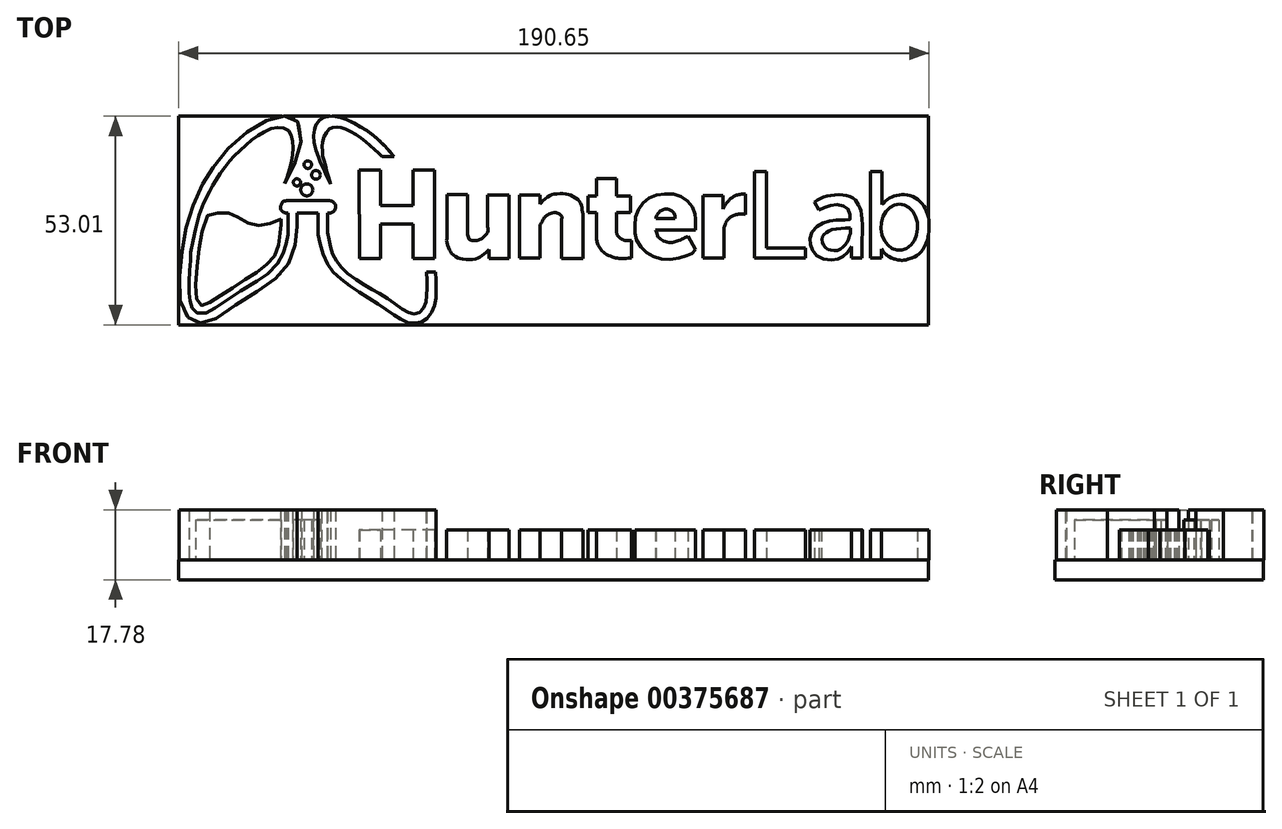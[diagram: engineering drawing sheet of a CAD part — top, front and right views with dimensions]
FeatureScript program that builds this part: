
annotation { "Feature Type Name" : "Feature", "Feature Type Description" : "" }
export const myFeature = defineFeature(function(context is Context, id is Id, definition is map)
    precondition{}
    {
        {
            var Q0;
            Q0=qCreatedBy(makeId("Top.planeOp"),FACE);
            var sketch = newSketch(context, id + "F0", { "sketchPlane" : qUnion([Q0])});
            skLineSegment(sketch, "E0.bottom", {"start": v(-95.8, -13.92) * mm, "end": v(94.76, -13.92) * mm});
            skLineSegment(sketch, "E0.top", {"start": v(-95.8, 39.08) * mm, "end": v(94.76, 39.08) * mm});
            skLineSegment(sketch, "E0.left", {"start": v(-95.8, -13.92) * mm, "end": v(-95.8, 39.08) * mm});
            skLineSegment(sketch, "E0.right", {"start": v(94.76, -13.92) * mm, "end": v(94.76, 39.08) * mm});
            skSolve(sketch);
        }
        {
            var Q0;
            Q0 = qSketchRegion(id + "F0", true);
            extrude(context, id + "F1", {"entities" : qUnion([Q0]), "oppositeDirection" : true, "depth" : 5.08 * mm});
        }
        {
            var Q0;
            Q0=qCreatedBy(makeId("Top.planeOp"),FACE);
            var sketch = newSketch(context, id + "F2", { "sketchPlane" : qUnion([Q0])});
            skLineSegment(sketch, "E1", {"start": v(-49.96, 25.38) * mm, "end": v(-44.45, 25.38) * mm});
            skLineSegment(sketch, "E2", {"start": v(-44.45, 25.38) * mm, "end": v(-44.45, 16.38) * mm});
            skLineSegment(sketch, "E3", {"start": v(-44.45, 16.38) * mm, "end": v(-36.19, 16.38) * mm});
            skLineSegment(sketch, "E4", {"start": v(-36.19, 16.38) * mm, "end": v(-36.19, 25.38) * mm});
            skLineSegment(sketch, "E5", {"start": v(-36.19, 25.38) * mm, "end": v(-30.8, 25.38) * mm});
            skLineSegment(sketch, "E6", {"start": v(-30.8, 25.38) * mm, "end": v(-30.8, 2.94) * mm});
            skLineSegment(sketch, "E7", {"start": v(-30.8, 2.94) * mm, "end": v(-36.19, 2.94) * mm});
            skLineSegment(sketch, "E8", {"start": v(-36.19, 2.94) * mm, "end": v(-36.19, 11.68) * mm});
            skLineSegment(sketch, "E9", {"start": v(-36.19, 11.68) * mm, "end": v(-44.45, 11.68) * mm});
            skLineSegment(sketch, "E10", {"start": v(-44.45, 11.68) * mm, "end": v(-44.45, 2.94) * mm});
            skLineSegment(sketch, "E11", {"start": v(-44.45, 2.94) * mm, "end": v(-49.84, 2.94) * mm});
            skLineSegment(sketch, "E12", {"start": v(-49.84, 2.94) * mm, "end": v(-49.96, 25.38) * mm});
            skLineSegment(sketch, "E13", {"start": v(-22.34, 19.15) * mm, "end": v(-27.62, 19.15) * mm});
            skLineSegment(sketch, "E14", {"start": v(-27.62, 19.15) * mm, "end": v(-27.62, 7.97) * mm});
            skLineSegment(sketch, "E15", {"start": v(-22.34, 19.15) * mm, "end": v(-22.34, 9.02) * mm});
            skLineSegment(sketch, "E16", {"start": v(-17.24, 10.98) * mm, "end": v(-17.24, 19.09) * mm});
            skLineSegment(sketch, "E17", {"start": v(-17.24, 19.09) * mm, "end": v(-11.9, 19.09) * mm});
            skLineSegment(sketch, "E18", {"start": v(-11.9, 19.09) * mm, "end": v(-11.9, 2.93) * mm});
            skLineSegment(sketch, "E19", {"start": v(-11.9, 2.93) * mm, "end": v(-16.94, 2.93) * mm});
            skLineSegment(sketch, "E20", {"start": v(-16.94, 2.93) * mm, "end": v(-16.94, 5.2) * mm});
            skLineSegment(sketch, "E21", {"start": v(-3.91, 16.75) * mm, "end": v(-3.91, 19.03) * mm});
            skLineSegment(sketch, "E22", {"start": v(-3.91, 19.03) * mm, "end": v(-9.13, 19.03) * mm});
            skLineSegment(sketch, "E23", {"start": v(-9.13, 19.03) * mm, "end": v(-9.13, 3) * mm});
            skLineSegment(sketch, "E24", {"start": v(-9.13, 3) * mm, "end": v(-3.91, 3) * mm});
            skLineSegment(sketch, "E25", {"start": v(-3.91, 3) * mm, "end": v(-3.91, 11.53) * mm});
            skLineSegment(sketch, "E26", {"start": v(1.55, 12.95) * mm, "end": v(1.55, 2.93) * mm});
            skLineSegment(sketch, "E27", {"start": v(1.55, 2.93) * mm, "end": v(6.9, 2.93) * mm});
            skLineSegment(sketch, "E28", {"start": v(6.9, 2.93) * mm, "end": v(6.9, 14.18) * mm});
            skLineSegment(sketch, "E29", {"start": v(15.5, 9.36) * mm, "end": v(15.5, 14.66) * mm});
            skLineSegment(sketch, "E30", {"start": v(15.5, 14.66) * mm, "end": v(19, 14.66) * mm});
            skLineSegment(sketch, "E31", {"start": v(19, 14.66) * mm, "end": v(19, 18.73) * mm});
            skLineSegment(sketch, "E32", {"start": v(19, 18.73) * mm, "end": v(15.5, 18.73) * mm});
            skLineSegment(sketch, "E33", {"start": v(15.5, 18.73) * mm, "end": v(15.5, 23.29) * mm});
            skLineSegment(sketch, "E34", {"start": v(15.5, 23.29) * mm, "end": v(10.42, 23.29) * mm});
            skLineSegment(sketch, "E35", {"start": v(10.42, 23.29) * mm, "end": v(10.42, 18.73) * mm});
            skLineSegment(sketch, "E36", {"start": v(10.42, 18.73) * mm, "end": v(8.22, 18.73) * mm});
            skLineSegment(sketch, "E37", {"start": v(8.22, 18.73) * mm, "end": v(8.22, 14.66) * mm});
            skLineSegment(sketch, "E38", {"start": v(8.22, 14.66) * mm, "end": v(10.42, 14.66) * mm});
            skLineSegment(sketch, "E39", {"start": v(10.42, 14.66) * mm, "end": v(10.42, 7.8) * mm});
            skLineSegment(sketch, "E40", {"start": v(19.22, 7.53) * mm, "end": v(19.22, 3.01) * mm});
            skLineSegment(sketch, "E41", {"start": v(25.43, 10.11) * mm, "end": v(35.5, 10.11) * mm});
            skLineSegment(sketch, "E42", {"start": v(35.5, 10.11) * mm, "end": v(35.5, 13.01) * mm});
            skLineSegment(sketch, "E43", {"start": v(25.48, 13.06) * mm, "end": v(30.32, 13.06) * mm});
            skLineSegment(sketch, "E44", {"start": v(33.65, 8.61) * mm, "end": v(35.56, 5.18) * mm});
            skLineSegment(sketch, "E45", {"start": v(42.73, 10.52) * mm, "end": v(42.73, 2.99) * mm});
            skLineSegment(sketch, "E46", {"start": v(42.73, 2.99) * mm, "end": v(37.44, 2.99) * mm});
            skLineSegment(sketch, "E47", {"start": v(37.44, 2.99) * mm, "end": v(37.44, 18.97) * mm});
            skLineSegment(sketch, "E48", {"start": v(37.44, 18.97) * mm, "end": v(42.48, 18.97) * mm});
            skLineSegment(sketch, "E49", {"start": v(42.48, 18.97) * mm, "end": v(42.48, 15.46) * mm});
            skLineSegment(sketch, "E50", {"start": v(48.23, 19.32) * mm, "end": v(48.23, 14.13) * mm});
            skLineSegment(sketch, "E51", {"start": v(50.52, 24.97) * mm, "end": v(53.57, 24.97) * mm});
            skLineSegment(sketch, "E52", {"start": v(53.57, 24.97) * mm, "end": v(53.57, 5.64) * mm});
            skLineSegment(sketch, "E53", {"start": v(53.57, 5.64) * mm, "end": v(63.45, 5.64) * mm});
            skLineSegment(sketch, "E54", {"start": v(63.45, 5.64) * mm, "end": v(63.45, 2.99) * mm});
            skLineSegment(sketch, "E55", {"start": v(63.45, 2.99) * mm, "end": v(50.52, 2.99) * mm});
            skLineSegment(sketch, "E56", {"start": v(50.52, 2.99) * mm, "end": v(50.52, 24.97) * mm});
            skLineSegment(sketch, "E57", {"start": v(65.79, 17.29) * mm, "end": v(66.85, 15.2) * mm});
            skLineSegment(sketch, "E58", {"start": v(75.17, 2.99) * mm, "end": v(77.8, 2.99) * mm});
            skLineSegment(sketch, "E59", {"start": v(82.93, 24.97) * mm, "end": v(79.98, 24.97) * mm});
            skLineSegment(sketch, "E60", {"start": v(79.98, 24.97) * mm, "end": v(79.98, 2.99) * mm});
            skLineSegment(sketch, "E61", {"start": v(79.98, 2.99) * mm, "end": v(82.78, 2.99) * mm});
            skLineSegment(sketch, "E62", {"start": v(82.78, 2.99) * mm, "end": v(82.78, 5.28) * mm});
            skLineSegment(sketch, "E63", {"start": v(82.93, 24.97) * mm, "end": v(82.93, 16.58) * mm});
            skFitSpline(sketch, "E64", {"points": [v(82.93, 16.58) * mm, v(84.56, 18.15) * mm, v(86.65, 18.97) * mm, v(89.2, 19.07) * mm, v(91.94, 17.95) * mm, v(93.88, 15.66) * mm, v(94.86, 12.7) * mm, v(94.86, 9.8) * mm, v(94.33, 7.26) * mm, v(92.7, 4.52) * mm, v(91.03, 3.3) * mm, v(88.18, 2.48) * mm, v(85.89, 2.84) * mm, v(84.1, 3.8) * mm, v(82.78, 5.28) * mm], "startDerivative": vector(22.65, 26) * mm, "endDerivative": vector(-19.5, 25.28) * mm});
            skEllipse(sketch, "E65", {"center": v(87.31, 10.88) * mm, "majorRadius": 5.87 * mm, "minorRadius": 4.66 * mm, "majorAxis": v(0, 1)});
            skFitSpline(sketch, "E66", {"points": [v(65.79, 17.29) * mm, v(67.57, 18.3) * mm, v(69.96, 18.97) * mm, v(72.96, 19.07) * mm, v(75.15, 18.46) * mm, v(76.52, 17.29) * mm, v(77.27, 15.83) * mm, v(77.8, 13.58) * mm, v(77.8, 2.99) * mm], "startDerivative": vector(16.24, 10.48) * mm, "endDerivative": vector(-0.09, -55.71) * mm});
            skFitSpline(sketch, "E67", {"points": [v(66.85, 15.2) * mm, v(68.62, 16) * mm, v(70.4, 16.52) * mm, v(72.6, 16.46) * mm, v(74.07, 15.68) * mm, v(74.75, 14.31) * mm, v(74.8, 12.9) * mm, v(74.23, 12.74) * mm, v(71.19, 12.74) * mm, v(68.93, 12.32) * mm, v(66.85, 11.43) * mm, v(65.16, 9.64) * mm, v(64.63, 7.55) * mm, v(64.84, 5.92) * mm, v(65.78, 4.19) * mm, v(68.1, 2.82) * mm, v(70.93, 2.61) * mm, v(72.66, 3.24) * mm, v(73.81, 4.08) * mm, v(75.17, 5.92) * mm], "startDerivative": vector(33.79, 15.82) * mm, "endDerivative": vector(21.23, 32.82) * mm});
            skLineSegment(sketch, "E68", {"start": v(75.17, 5.92) * mm, "end": v(75.17, 2.99) * mm});
            skFitSpline(sketch, "E69", {"points": [v(74.91, 10.64) * mm, v(71.76, 10.48) * mm, v(69.56, 10.01) * mm, v(68.56, 9.33) * mm, v(67.83, 8.54) * mm, v(67.67, 7.34) * mm, v(68.1, 6.29) * mm, v(69.09, 5.34) * mm, v(70.2, 5.03) * mm, v(71.71, 5.03) * mm, v(72.81, 5.66) * mm, v(73.81, 6.65) * mm, v(74.5, 8.02) * mm, v(74.91, 9.33) * mm, v(74.91, 9.28) * mm], "startDerivative": vector(-28.78, -0.8) * mm, "endDerivative": vector(-4.05, -5.26) * mm});
            skLineSegment(sketch, "E70", {"start": v(74.91, 10.64) * mm, "end": v(74.91, 9.33) * mm});
            skFitSpline(sketch, "E71", {"points": [v(42.48, 15.46) * mm, v(43.53, 17.16) * mm, v(44.95, 18.46) * mm, v(46.25, 19.08) * mm, v(48.23, 19.32) * mm], "startDerivative": vector(3.6, 6.76) * mm, "endDerivative": vector(8.08, 0.55) * mm});
            skFitSpline(sketch, "E72", {"points": [v(48.23, 14.13) * mm, v(46.07, 14.13) * mm, v(44.52, 13.5) * mm, v(43.28, 12.14) * mm, v(42.73, 10.52) * mm], "startDerivative": vector(-8.11, 0.9) * mm, "endDerivative": vector(-2.19, -5.73) * mm});
            skFitSpline(sketch, "E73", {"points": [v(35.5, 13.01) * mm, v(35.5, 14) * mm, v(34.49, 16.41) * mm, v(32.63, 18.21) * mm, v(29.9, 19.26) * mm, v(26.62, 19.2) * mm, v(23.71, 18.27) * mm, v(21.73, 16.41) * mm, v(20.3, 13.69) * mm, v(20.12, 10.66) * mm, v(20.37, 8.24) * mm, v(21.8, 5.64) * mm, v(23.96, 3.84) * mm, v(26.87, 2.8) * mm, v(30.28, 2.8) * mm, v(33.62, 3.72) * mm, v(34.61, 4.21) * mm, v(35.56, 5.18) * mm], "startDerivative": vector(2.92, 23.87) * mm, "endDerivative": vector(15.92, 25.8) * mm});
            skFitSpline(sketch, "E74", {"points": [v(33.65, 8.61) * mm, v(32.38, 8) * mm, v(31.02, 7.37) * mm, v(29.84, 7.06) * mm, v(28.3, 7.06) * mm, v(26.93, 7.68) * mm, v(25.94, 8.61) * mm, v(25.43, 10.11) * mm], "startDerivative": vector(-8.12, -5.44) * mm, "endDerivative": vector(-4.59, 9.54) * mm});
            skFitSpline(sketch, "E75", {"points": [v(15.5, 9.36) * mm, v(15.79, 8.67) * mm, v(16.73, 7.86) * mm, v(17.84, 7.5) * mm, v(19.22, 7.53) * mm], "startDerivative": vector(0.88, -3.35) * mm, "endDerivative": vector(5.13, 0.44) * mm});
            skFitSpline(sketch, "E76", {"points": [v(10.42, 7.8) * mm, v(10.62, 6.68) * mm, v(11.4, 5.33) * mm, v(12.66, 4.15) * mm, v(14.64, 3.27) * mm, v(16.09, 2.98) * mm, v(19.22, 3.01) * mm], "startDerivative": vector(0.64, -8.95) * mm, "endDerivative": vector(16.04, 0.67) * mm});
            skFitSpline(sketch, "E77", {"points": [v(-3.91, 16.75) * mm, v(-3.07, 17.74) * mm, v(-1.3, 18.95) * mm, v(0, 19.3) * mm, v(2.44, 19.35) * mm, v(3.95, 18.95) * mm, v(5.72, 17.79) * mm, v(6.42, 16.75) * mm, v(6.73, 15.42) * mm, v(6.9, 14.18) * mm], "startDerivative": vector(7.09, 9.57) * mm, "endDerivative": vector(1.61, -12.4) * mm});
            skFitSpline(sketch, "E78", {"points": [v(1.55, 12.95) * mm, v(1.55, 13.65) * mm, v(1.02, 14.18) * mm, v(0, 14.6) * mm, v(-1.75, 14.18) * mm, v(-2.56, 13.65) * mm, v(-3.12, 12.95) * mm, v(-3.42, 12.24) * mm, v(-3.91, 11.53) * mm], "startDerivative": vector(1.14, 7.02) * mm, "endDerivative": vector(-4.71, -5.81) * mm});
            skFitSpline(sketch, "E79", {"points": [v(-17.24, 10.98) * mm, v(-17.24, 9.86) * mm, v(-18.25, 8.41) * mm, v(-19.13, 7.8) * mm, v(-20.35, 7.46) * mm, v(-21.23, 7.5) * mm, v(-21.92, 7.8) * mm, v(-22.34, 9.02) * mm], "startDerivative": vector(1.28, -7.5) * mm, "endDerivative": vector(-1.92, 8.98) * mm});
            skFitSpline(sketch, "E80", {"points": [v(-27.62, 7.97) * mm, v(-27.62, 6.84) * mm, v(-27, 5.23) * mm, v(-26.42, 4.25) * mm, v(-25.07, 3.2) * mm, v(-23.4, 2.77) * mm, v(-20.58, 2.77) * mm, v(-19.03, 3.4) * mm, v(-17.72, 4.44) * mm, v(-16.94, 5.2) * mm], "startDerivative": vector(-1.32, -11.42) * mm, "endDerivative": vector(7.85, 7.93) * mm});
            skFitSpline(sketch, "E81", {"points": [v(25.48, 13.06) * mm, v(25.72, 13.85) * mm, v(26.5, 14.87) * mm, v(27.26, 15.33) * mm, v(28.05, 15.46) * mm, v(28.92, 15.35) * mm, v(29.6, 14.95) * mm, v(30.16, 14.22) * mm, v(30.32, 13.56) * mm, v(30.32, 13.06) * mm], "startDerivative": vector(1.4, 6.81) * mm, "endDerivative": vector(-0.2, -5.58) * mm});
            skLineSegment(sketch, "E82.bottom", {"start": v(-95.64, 39.01) * mm, "end": v(94.86, 39.01) * mm});
            skLineSegment(sketch, "E82.top", {"start": v(-95.64, -13.6) * mm, "end": v(94.86, -13.6) * mm});
            skLineSegment(sketch, "E82.left", {"start": v(-95.64, 39.01) * mm, "end": v(-95.64, -13.6) * mm});
            skLineSegment(sketch, "E82.right", {"start": v(94.86, 39.01) * mm, "end": v(94.86, -13.6) * mm});
            skSolve(sketch);
        }
        {
            var Q0;
            Q0=makeQuery(id+"F2.imprint","IMPRINT",FACE,{"disambiguationData":[TD([[makeQuery(id+"F2.imprint","IMPRINT",EDGE,{"derivedFrom":sQuery(id+"F2.wireOp",EDGE,"E1")}),-1.0]])]});
            var Q1;
            Q1=makeQuery(id+"F2.imprint","IMPRINT",FACE,{"disambiguationData":[TD([[makeQuery(id+"F2.imprint","IMPRINT",EDGE,{"derivedFrom":sQuery(id+"F2.wireOp",EDGE,"E13")}),1.0]])]});
            var Q2;
            Q2=makeQuery(id+"F2.imprint","IMPRINT",FACE,{"disambiguationData":[TD([[makeQuery(id+"F2.imprint","IMPRINT",EDGE,{"derivedFrom":sQuery(id+"F2.wireOp",EDGE,"E21")}),1.0]])]});
            var Q3;
            Q3=makeQuery(id+"F2.imprint","IMPRINT",FACE,{"disambiguationData":[TD([[makeQuery(id+"F2.imprint","IMPRINT",EDGE,{"derivedFrom":sQuery(id+"F2.wireOp",EDGE,"E29")}),1.0]])]});
            var Q4;
            Q4=makeQuery(id+"F2.imprint","IMPRINT",FACE,{"disambiguationData":[TD([[makeQuery(id+"F2.imprint","IMPRINT",EDGE,{"derivedFrom":sQuery(id+"F2.wireOp",EDGE,"E45")}),-1.0]])]});
            var Q5;
            Q5=makeQuery(id+"F2.imprint","IMPRINT",FACE,{"disambiguationData":[TD([[makeQuery(id+"F2.imprint","IMPRINT",EDGE,{"derivedFrom":sQuery(id+"F2.wireOp",EDGE,"E41")}),1.0]])]});
            extrude(context, id + "F3", {"entities" : qUnion([Q0, Q1, Q2, Q3, Q4, Q5]), "operationType" : NewBodyOperationType.ADD, "depth" : 7.62 * mm});
        }
        {
            var Q0;
            Q0=makeQuery(id+"F2.imprint","IMPRINT",FACE,{"disambiguationData":[TD([[makeQuery(id+"F2.imprint","IMPRINT",EDGE,{"derivedFrom":sQuery(id+"F2.wireOp",EDGE,"E51")}),-1.0]])]});
            var Q1;
            Q1=makeQuery(id+"F2.imprint","IMPRINT",FACE,{"disambiguationData":[TD([[makeQuery(id+"F2.imprint","IMPRINT",EDGE,{"derivedFrom":sQuery(id+"F2.wireOp",EDGE,"E57")}),1.0]])]});
            var Q2;
            Q2=makeQuery(id+"F2.imprint","IMPRINT",FACE,{"disambiguationData":[TD([[makeQuery(id+"F2.imprint","IMPRINT",EDGE,{"derivedFrom":sQuery(id+"F2.wireOp",EDGE,"E59")}),1.0]])]});
            extrude(context, id + "F4", {"entities" : qUnion([Q0, Q1, Q2]), "operationType" : NewBodyOperationType.ADD, "depth" : 7.62 * mm});
        }
        {
            var Q0;
            Q0=makeQuery(id+"F2.imprint","IMPRINT",FACE,{"disambiguationData":[TD([[makeQuery(id+"F2.imprint","IMPRINT",EDGE,{"derivedFrom":sQuery(id+"F2.wireOp",EDGE,"E1")}),1.0]])]});
            var sketch = newSketch(context, id + "F5", { "sketchPlane" : qUnion([Q0])});
            skLineSegment(sketch, "E83", {"start": v(-68.34, 17.61) * mm, "end": v(-58.06, 17.61) * mm});
            skLineSegment(sketch, "E84", {"start": v(-67.95, 14.5) * mm, "end": v(-67.95, 11.06) * mm});
            skLineSegment(sketch, "E85", {"start": v(-57.94, 14.5) * mm, "end": v(-57.94, 11.36) * mm});
            skLineSegment(sketch, "E86", {"start": v(-65.7, 11.06) * mm, "end": v(-65.7, 14.5) * mm});
            skLineSegment(sketch, "E87", {"start": v(-65.7, 14.5) * mm, "end": v(-60.32, 14.5) * mm});
            skLineSegment(sketch, "E88", {"start": v(-60.32, 14.5) * mm, "end": v(-60.32, 11.26) * mm});
            skFitSpline(sketch, "E89", {"points": [v(-68.34, 17.61) * mm, v(-69.09, 17.46) * mm, v(-69.64, 16.83) * mm, v(-69.86, 16.05) * mm, v(-69.83, 15.46) * mm, v(-69.42, 14.87) * mm, v(-68.72, 14.54) * mm, v(-67.95, 14.5) * mm], "startDerivative": vector(-5.2, -2.07) * mm, "endDerivative": vector(5.37, 0.05) * mm});
            skFitSpline(sketch, "E90", {"points": [v(-57.94, 14.5) * mm, v(-57.16, 14.5) * mm, v(-56.52, 14.8) * mm, v(-56.05, 15.33) * mm, v(-55.97, 16.62) * mm, v(-56.3, 17.09) * mm, v(-56.85, 17.45) * mm, v(-57.46, 17.61) * mm, v(-58.06, 17.61) * mm], "startDerivative": vector(6.89, -0.67) * mm, "endDerivative": vector(-5.35, -0.27) * mm});
            skFitSpline(sketch, "E91", {"points": [v(-67.95, 11.06) * mm, v(-67.95, 9.88) * mm, v(-68.13, 8.36) * mm, v(-68.56, 6.34) * mm, v(-69.12, 4.33) * mm, v(-70.12, 2.36) * mm, v(-73.05, -0.87) * mm, v(-75.55, -2.54) * mm, v(-81.55, -6.33) * mm, v(-85.1, -8.77) * mm, v(-88.16, -10.69) * mm, v(-89.3, -11) * mm, v(-90.94, -11) * mm, v(-91.74, -10.41) * mm, v(-92.4, -9.55) * mm, v(-92.76, -8.43) * mm, v(-92.92, -7.3) * mm, v(-93.07, -5.84) * mm, v(-93.1, -3.37) * mm, v(-93.07, -0.96) * mm, v(-92.86, 1.6) * mm, v(-92.76, 2.96) * mm, v(-92.7, 4.23) * mm, v(-92.2, 7.2) * mm, v(-91.68, 9.64) * mm, v(-90.57, 13.87) * mm, v(-89.49, 16.8) * mm, v(-87.96, 19.99) * mm], "startDerivative": vector(1.14, -43.6) * mm, "endDerivative": vector(35.58, 72.1) * mm});
            skFitSpline(sketch, "E92", {"points": [v(-68.93, 21.94) * mm, v(-67.66, 23.8) * mm, v(-66.4, 26.83) * mm, v(-65.53, 29.23) * mm, v(-64.67, 32.63) * mm, v(-64.67, 35.3) * mm, v(-65.3, 37.39) * mm, v(-66.53, 38.52) * mm, v(-67.48, 38.93) * mm, v(-68.16, 39.02) * mm, v(-69.88, 39.06) * mm, v(-71.55, 38.6) * mm, v(-73.64, 37.84) * mm, v(-75.9, 36.7) * mm, v(-78.53, 34.94) * mm, v(-81.16, 32.81) * mm, v(-83.7, 30.23) * mm, v(-85.73, 27.87) * mm, v(-87.5, 25.43) * mm, v(-88.18, 24.34) * mm, v(-89.67, 21.94) * mm, v(-90.76, 19.63) * mm, v(-92.12, 16.5) * mm, v(-93.25, 13.15) * mm, v(-93.88, 10.7) * mm, v(-94.56, 7.63) * mm, v(-94.97, 4.5) * mm, v(-95.33, 0.75) * mm, v(-95.56, -2.97) * mm, v(-95.56, -6.73) * mm, v(-95.33, -8.36) * mm, v(-94.65, -10.67) * mm, v(-93.34, -12.12) * mm, v(-92.61, -12.75) * mm, v(-91.53, -13.25) * mm, v(-90.67, -13.39) * mm, v(-89.4, -13.43) * mm, v(-88.08, -13.11) * mm, v(-86.54, -12.43) * mm, v(-83.83, -10.85) * mm, v(-81.47, -9.04) * mm, v(-78.08, -6.9) * mm, v(-75.45, -5.2) * mm, v(-73, -3.6) * mm, v(-70.87, -1.93) * mm, v(-69.42, -0.57) * mm, v(-68.16, 1.1) * mm, v(-67.07, 3.42) * mm, v(-66.53, 5.23) * mm, v(-66.03, 7.13) * mm, v(-65.8, 8.67) * mm, v(-65.7, 11.06) * mm], "startDerivative": vector(68.15, 87.24) * mm, "endDerivative": vector(3.62, 129.17) * mm});
            skFitSpline(sketch, "E93", {"points": [v(-60.32, 11.26) * mm, v(-60.32, 8.96) * mm, v(-59.76, 6.3) * mm, v(-58.55, 2.66) * mm, v(-57.04, 0) * mm, v(-54.73, -2.14) * mm, v(-51.7, -4.45) * mm, v(-48.6, -6.38) * mm, v(-45.34, -8.5) * mm, v(-42.84, -10.2) * mm, v(-40.69, -11.68) * mm, v(-39.36, -12.48) * mm, v(-37.58, -13.3) * mm, v(-36.45, -13.46) * mm, v(-34.82, -13.46) * mm, v(-33.42, -12.9) * mm, v(-32.36, -11.95) * mm, v(-31.3, -10.47) * mm, v(-30.7, -8.96) * mm, v(-30.43, -7.25) * mm, v(-30.4, -5.28) * mm, v(-30.4, -2.48) * mm, v(-30.46, -0.56) * mm], "startDerivative": vector(-2.67, -49.82) * mm, "endDerivative": vector(-2.24, 43.27) * mm});
            skFitSpline(sketch, "E94", {"points": [v(-57.94, 11.36) * mm, v(-57.94, 9.63) * mm, v(-57.64, 8.06) * mm, v(-57.29, 6.06) * mm, v(-56.82, 4.31) * mm, v(-55.78, 2.42) * mm, v(-54.43, 0.63) * mm, v(-52.85, -0.87) * mm, v(-49.78, -2.98) * mm, v(-47.35, -4.48) * mm, v(-45.28, -5.7) * mm, v(-42.84, -7.13) * mm, v(-40.83, -8.6) * mm, v(-38.54, -10.18) * mm, v(-37.1, -10.93) * mm, v(-36, -11.11) * mm, v(-34.93, -11.07) * mm, v(-34.1, -10.38) * mm, v(-33.32, -9.32) * mm, v(-32.82, -7.95) * mm, v(-32.75, -6.5) * mm, v(-32.72, -4.67) * mm, v(-32.71, -2.8) * mm, v(-32.81, -0.56) * mm], "startDerivative": vector(-2, -43.26) * mm, "endDerivative": vector(-2.63, 49.7) * mm});
            skLineSegment(sketch, "E95", {"start": v(-32.81, -0.56) * mm, "end": v(-30.46, -0.56) * mm});
            skLineSegment(sketch, "E96", {"start": v(-44.1, 28.8) * mm, "end": v(-41.04, 28.8) * mm});
            skFitSpline(sketch, "E97", {"points": [v(-41.04, 28.8) * mm, v(-43.35, 31.44) * mm, v(-46.9, 34.61) * mm, v(-50.23, 36.77) * mm, v(-54, 38.54) * mm, v(-56.1, 39.03) * mm, v(-58.46, 38.92) * mm, v(-60.34, 37.68) * mm, v(-61.26, 35.8) * mm, v(-61.42, 32.84) * mm, v(-60.34, 28.8) * mm, v(-59.22, 26.28) * mm, v(-57.23, 21.87) * mm], "startDerivative": vector(-24.59, 29.7) * mm, "endDerivative": vector(21.06, -47.4) * mm});
            skFitSpline(sketch, "E98", {"points": [v(-44.1, 28.8) * mm, v(-45.4, 30.04) * mm, v(-47.17, 31.66) * mm, v(-49.1, 33.27) * mm, v(-51.3, 34.78) * mm, v(-53.4, 35.8) * mm, v(-54.8, 36.23) * mm, v(-56.1, 36.28) * mm, v(-57.17, 36.01) * mm, v(-58.09, 35.2) * mm, v(-58.9, 33.75) * mm, v(-59.27, 31.76) * mm, v(-59.27, 30.37) * mm, v(-59.1, 28.8) * mm, v(-58.66, 27.23) * mm, v(-58.11, 25) * mm, v(-57.23, 21.87) * mm], "startDerivative": vector(-20.2, 19.59) * mm, "endDerivative": vector(11.71, -39.23) * mm});
            skFitSpline(sketch, "E99", {"points": [v(-68.93, 21.94) * mm, v(-68.16, 23.8) * mm, v(-67.3, 26.8) * mm, v(-66.87, 28.96) * mm, v(-66.66, 30.64) * mm, v(-66.78, 32.63) * mm, v(-67.15, 34.16) * mm, v(-67.66, 35.32) * mm, v(-68.93, 36.05) * mm, v(-70.27, 36.24) * mm, v(-72.1, 35.96) * mm, v(-74.11, 35.01) * mm, v(-76.07, 33.85) * mm, v(-78.06, 32.26) * mm, v(-79.86, 30.7) * mm, v(-81.81, 28.75) * mm, v(-83.04, 27.44) * mm, v(-84.65, 25.24) * mm, v(-86.15, 23.13) * mm, v(-87.13, 21.54) * mm, v(-87.96, 19.99) * mm], "startDerivative": vector(15.55, 34.4) * mm, "endDerivative": vector(-17.61, -33.71) * mm});
            skSolve(sketch);
        }
        {
            var Q0;
            Q0 = qSketchRegion(id + "F5", true);
            extrude(context, id + "F6", {"entities" : qUnion([Q0]), "operationType" : NewBodyOperationType.ADD, "depth" : 12.7 * mm});
        }
        {
            var Q0;
            Q0=makeQuery(id+"F2.imprint","IMPRINT",FACE,{"disambiguationData":[TD([[makeQuery(id+"F2.imprint","IMPRINT",EDGE,{"derivedFrom":sQuery(id+"F2.wireOp",EDGE,"E1")}),1.0]])]});
            var sketch = newSketch(context, id + "F7", { "sketchPlane" : qUnion([Q0])});
            skCircle(sketch, "E100", {"center": v(-63.22, 20.36) * mm, "radius": 1.54 * mm});
            skCircle(sketch, "E101", {"center": v(-60.88, 24.17) * mm, "radius": 1.1 * mm});
            skCircle(sketch, "E102", {"center": v(-65.73, 22.27) * mm, "radius": 0.92 * mm});
            skCircle(sketch, "E103", {"center": v(-62.96, 26.76) * mm, "radius": 0.97 * mm});
            skFitSpline(sketch, "E104", {"points": [v(-69.7, 12.93) * mm, v(-72.12, 11.98) * mm, v(-73.85, 11.55) * mm, v(-76.19, 11.37) * mm, v(-77.92, 11.9) * mm, v(-80, 13.02) * mm, v(-81.9, 14.05) * mm, v(-83.19, 14.49) * mm, v(-85.18, 14.57) * mm, v(-87.17, 14.14) * mm, v(-88.64, 13.62) * mm, v(-90.02, 8.52) * mm, v(-90.8, 4.03) * mm, v(-91.32, -1.77) * mm, v(-91.4, -6.18) * mm, v(-90.88, -8.16) * mm, v(-90.36, -8.86) * mm, v(-89.3, -9) * mm, v(-88.11, -8.41) * mm, v(-85.96, -7) * mm, v(-83.3, -5.37) * mm, v(-80.18, -3.22) * mm, v(-77.28, -1.44) * mm, v(-75.2, 0) * mm, v(-73.13, 1.6) * mm, v(-71.65, 3.24) * mm, v(-70.6, 5.46) * mm, v(-70.24, 7.32) * mm, v(-69.94, 9.91) * mm, v(-69.8, 11.46) * mm, v(-69.8, 11.6) * mm], "startDerivative": vector(-66.54, -31.72) * mm, "endDerivative": vector(0, -39.97) * mm});
            skLineSegment(sketch, "E105", {"start": v(-69.7, 12.93) * mm, "end": v(-69.8, 11.72) * mm});
            skLineSegment(sketch, "E106", {"start": v(-69.8, 11.72) * mm, "end": v(-69.8, 11.6) * mm});
            skSolve(sketch);
        }
        {
            var Q0;
            Q0=makeQuery(id+"F7.imprint","IMPRINT",FACE,{"disambiguationData":[TD([[makeQuery(id+"F7.imprint","IMPRINT",EDGE,{"derivedFrom":sQuery(id+"F7.wireOp",EDGE,"E102")}),1.0]])]});
            var Q1;
            Q1=makeQuery(id+"F7.imprint","IMPRINT",FACE,{"disambiguationData":[TD([[makeQuery(id+"F7.imprint","IMPRINT",EDGE,{"derivedFrom":sQuery(id+"F7.wireOp",EDGE,"E100")}),1.0]])]});
            var Q2;
            Q2=makeQuery(id+"F7.imprint","IMPRINT",FACE,{"disambiguationData":[TD([[makeQuery(id+"F7.imprint","IMPRINT",EDGE,{"derivedFrom":sQuery(id+"F7.wireOp",EDGE,"E101")}),1.0]])]});
            var Q3;
            Q3=makeQuery(id+"F7.imprint","IMPRINT",FACE,{"disambiguationData":[TD([[makeQuery(id+"F7.imprint","IMPRINT",EDGE,{"derivedFrom":sQuery(id+"F7.wireOp",EDGE,"E103")}),1.0]])]});
            var Q4;
            Q4=makeQuery(id+"F7.imprint","IMPRINT",FACE,{"disambiguationData":[TD([[makeQuery(id+"F7.imprint","IMPRINT",EDGE,{"derivedFrom":sQuery(id+"F7.wireOp",EDGE,"E104")}),1.0]])]});
            extrude(context, id + "F8", {"entities" : qUnion([Q0, Q1, Q2, Q3, Q4]), "operationType" : NewBodyOperationType.ADD, "depth" : 10.16 * mm});
        }
    });
